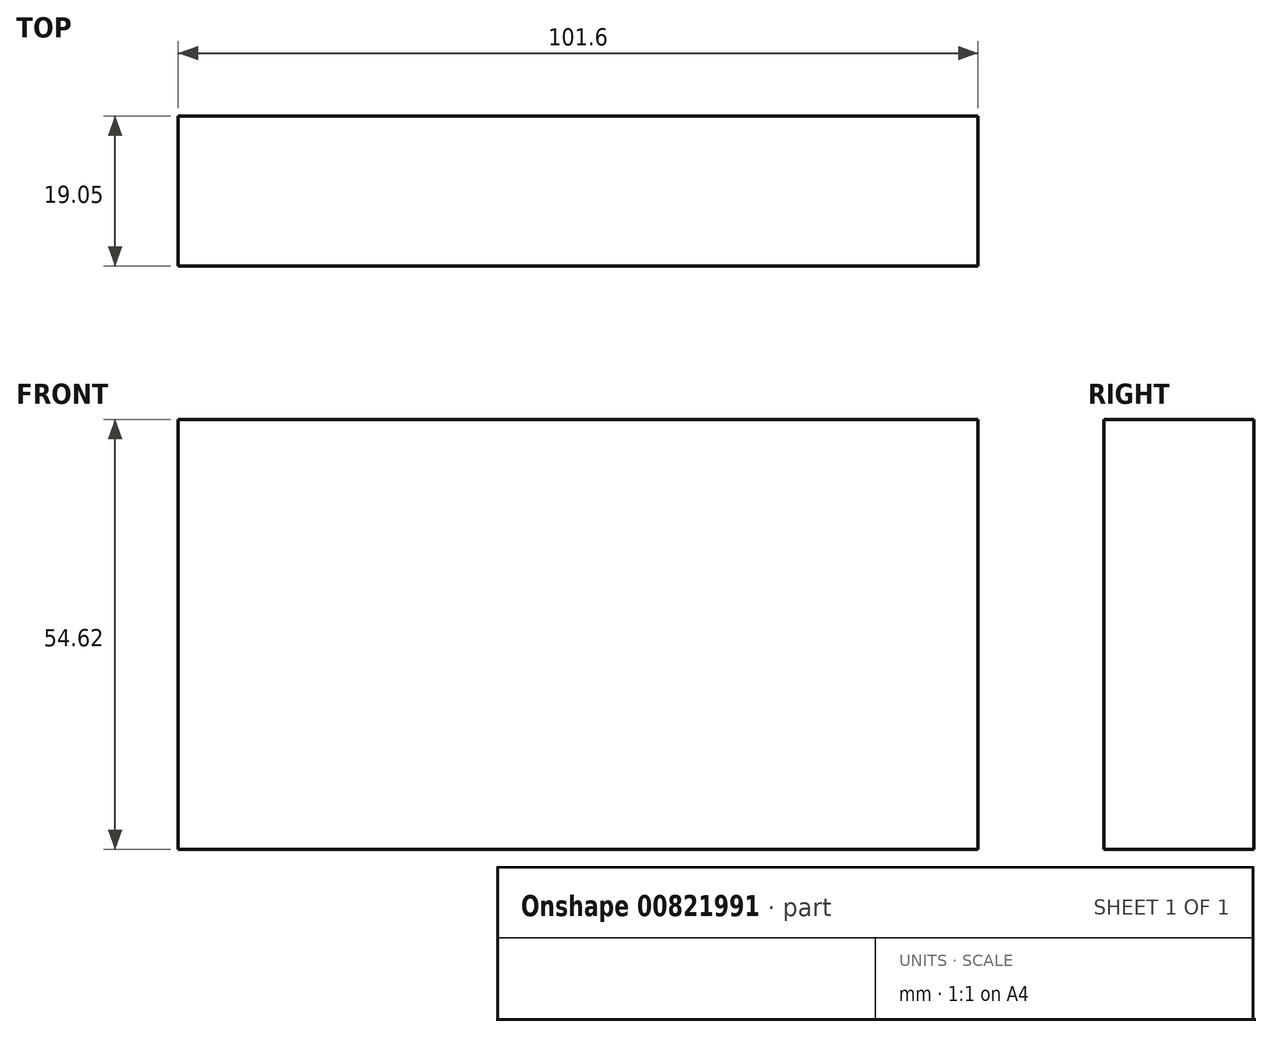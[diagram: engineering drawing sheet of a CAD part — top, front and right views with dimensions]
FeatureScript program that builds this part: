
annotation { "Feature Type Name" : "Feature", "Feature Type Description" : "" }
export const myFeature = defineFeature(function(context is Context, id is Id, definition is map)
    precondition{}
    {
        {
            var Q0;
            Q0=qCreatedBy(makeId("Front.planeOp"),FACE);
            var sketch = newSketch(context, id + "F0", { "sketchPlane" : qUnion([Q0])});
            skLineSegment(sketch, "E0", {"start": v(0, 0) * mm, "end": v(-50.8, 0) * mm});
            skLineSegment(sketch, "E1", {"start": v(0, 0) * mm, "end": v(50.8, 0) * mm});
            skLineSegment(sketch, "E2", {"start": v(50.8, 0) * mm, "end": v(50.8, 54.62) * mm});
            skLineSegment(sketch, "E3", {"start": v(50.8, 54.62) * mm, "end": v(-50.8, 54.62) * mm});
            skLineSegment(sketch, "E4", {"start": v(-50.8, 54.62) * mm, "end": v(-50.8, 0) * mm});
            skSolve(sketch);
        }
        {
            var Q0;
            Q0=makeQuery(id+"F0.imprint","IMPRINT",FACE,{"disambiguationData":[TD([[makeQuery(id+"F0.imprint","IMPRINT",EDGE,{"derivedFrom":sQuery(id+"F0.wireOp",EDGE,"E0")}),-1.0]])]});
            extrude(context, id + "F1", {"entities" : qUnion([Q0]), "depth" : 19.05 * mm, "offsetDistance" : 25.4 * mm});
        }
    });
